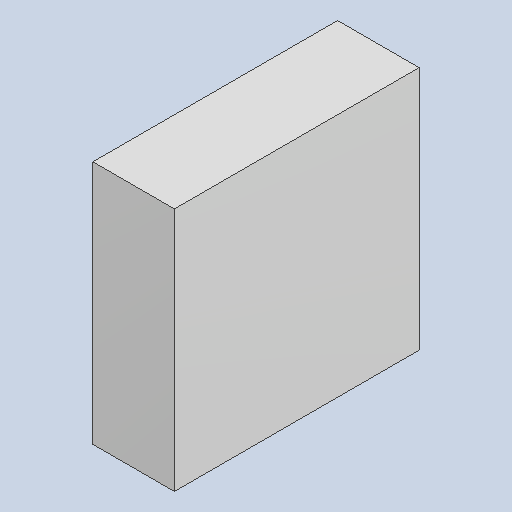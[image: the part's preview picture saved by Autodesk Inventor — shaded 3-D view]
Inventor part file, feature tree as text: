
AUTODESK INVENTOR PART (.ipt)
format: ipt  version: 2023.4 (Build 274418000, 418)  size: 81,408 bytes
history: native  units: mm
features: extrude x1
ambient origin geometry x8: Origin, YZ Plane, XZ Plane, XY Plane, X Axis, Y Axis, Z Axis, Center Point
bodies: Solid1 (feature_tree)
feature tree (1):
  extrude  "Extruded_12"  [1 undecoded]
note: 1 required parameter value undecoded (feature->parameter linkage not recoverable at this tier; creation-order binding heuristic only, values carry confidence <= 0.55)
